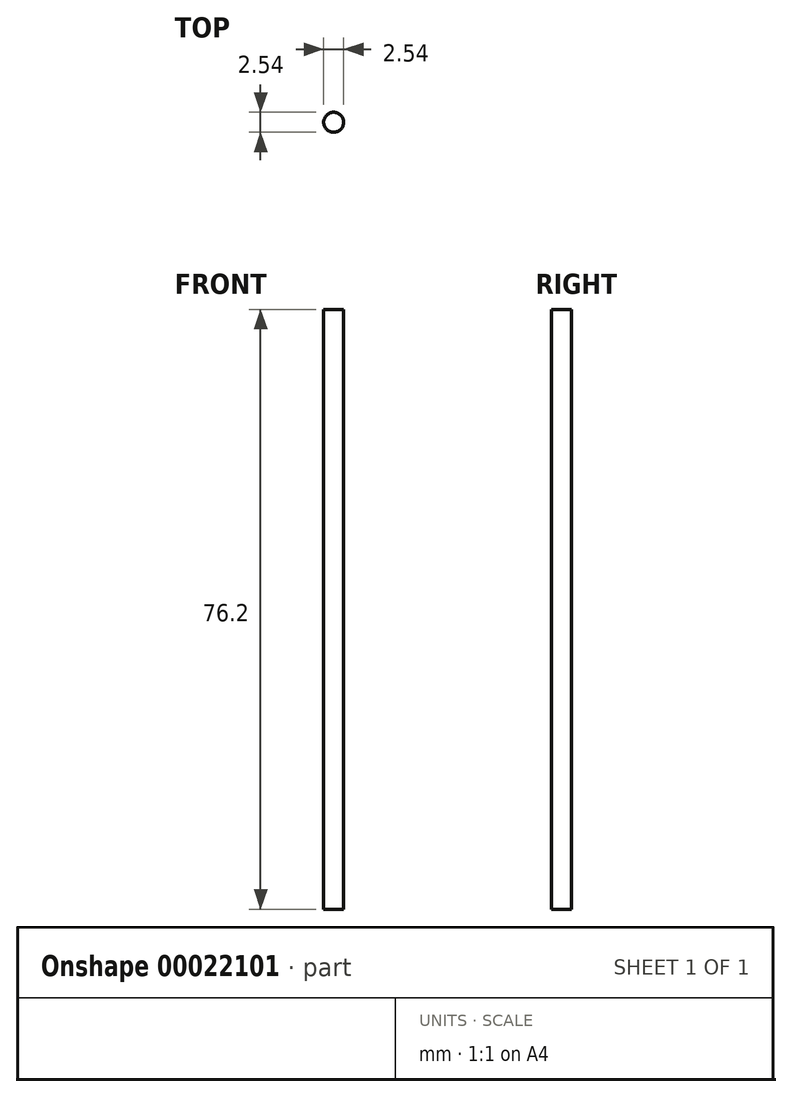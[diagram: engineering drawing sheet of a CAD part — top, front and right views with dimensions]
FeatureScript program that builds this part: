
annotation { "Feature Type Name" : "Feature", "Feature Type Description" : "" }
export const myFeature = defineFeature(function(context is Context, id is Id, definition is map)
    precondition{}
    {
        {
            var Q0;
            Q0=qCreatedBy(makeId("Front.planeOp"),FACE);
            var sketch = newSketch(context, id + "F0", { "sketchPlane" : qUnion([Q0])});
            skLineSegment(sketch, "E0.bottom", {"start": v(-37.5, 73.07) * mm, "end": v(-36.22, 73.07) * mm});
            skLineSegment(sketch, "E0.top", {"start": v(-37.5, -3.13) * mm, "end": v(-36.22, -3.13) * mm});
            skLineSegment(sketch, "E0.left", {"start": v(-37.5, 73.07) * mm, "end": v(-37.5, -3.13) * mm});
            skLineSegment(sketch, "E0.right", {"start": v(-36.22, 73.07) * mm, "end": v(-36.22, -3.13) * mm});
            skSolve(sketch);
        }
        {
            var Q0;
            Q0=makeQuery(id+"F0.imprint","IMPRINT",FACE,{"disambiguationData":[TD([[makeQuery(id+"F0.imprint","IMPRINT",EDGE,{"derivedFrom":sQuery(id+"F0.wireOp",EDGE,"E0.bottom")}),-1.0]])]});
            var Q1;
            Q1=sQuery(id+"F0.wireOp",EDGE,"E0.right");
            revolve(context, id + "F1", {"entities" : qUnion([Q0]), "axis" : qUnion([Q1]), "revolveType" : RevolveType.FULL});
        }
    });
